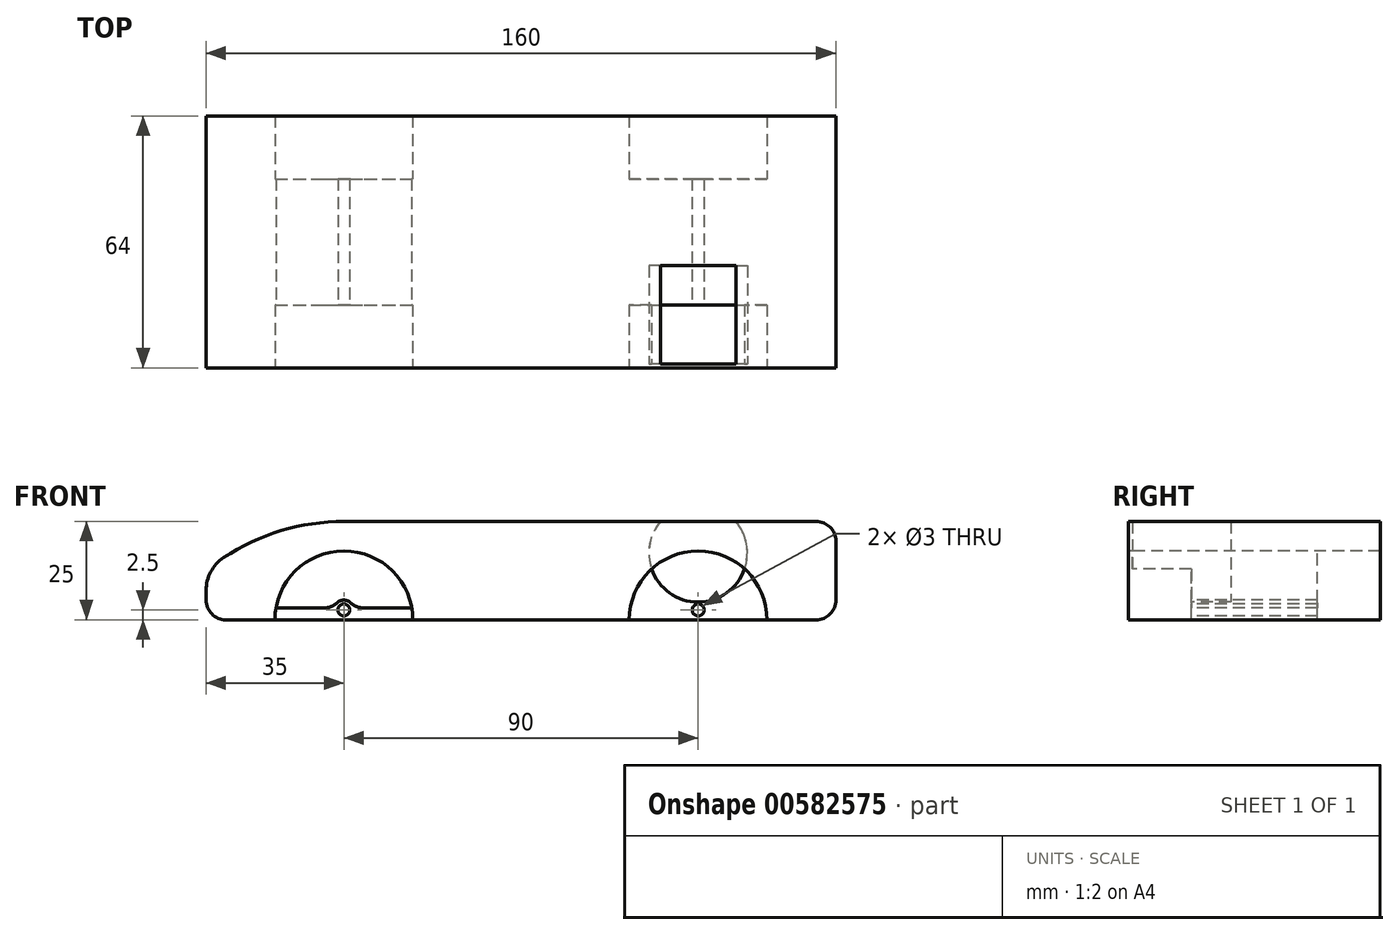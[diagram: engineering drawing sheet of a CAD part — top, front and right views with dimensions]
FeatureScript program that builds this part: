
annotation { "Feature Type Name" : "Feature", "Feature Type Description" : "" }
export const myFeature = defineFeature(function(context is Context, id is Id, definition is map)
    precondition{}
    {
        {
            var Q0;
            Q0=qCreatedBy(makeId("Front.planeOp"),FACE);
            var sketch = newSketch(context, id + "F0", { "sketchPlane" : qUnion([Q0])});
            skLineSegment(sketch, "E0.bottom", {"start": v(0, 0) * mm, "end": v(17.5, 0) * mm});
            skLineSegment(sketch, "E0.top", {"start": v(35, 25) * mm, "end": v(160, 25) * mm});
            skLineSegment(sketch, "E0.left", {"start": v(0, 0) * mm, "end": v(0, 12.5) * mm});
            skLineSegment(sketch, "E0.right", {"start": v(160, 0) * mm, "end": v(160, 25) * mm});
            skArc(sketch, "E1", {"start": v(52.5, 0) * mm, "mid": v(35, 17.5) * mm, "end": v(17.5, 0) * mm});
            skArc(sketch, "E2", {"start": v(142.5, 0) * mm, "mid": v(125, 17.5) * mm, "end": v(107.5, 0) * mm});
            skPoint(sketch, "E3", {"position": v(35, 25) * mm});
            skArc(sketch, "E4", {"start": v(35, 25) * mm, "mid": v(16.42, 21.78) * mm, "end": v(0, 12.5) * mm});
            skPoint(sketch, "E5.orphan", {"position": v(0, 25) * mm});
            skLineSegment(sketch, "E6.trimOffspring", {"start": v(52.5, 0) * mm, "end": v(107.5, 0) * mm});
            skLineSegment(sketch, "E7.trimOffspring", {"start": v(142.5, 0) * mm, "end": v(160, 0) * mm});
            skSolve(sketch);
        }
        {
            var Q0;
            Q0=makeQuery(id+"F0.imprint","IMPRINT",FACE,{"disambiguationData":[TD([[makeQuery(id+"F0.imprint","IMPRINT",EDGE,{"derivedFrom":sQuery(id+"F0.wireOp",EDGE,"E0.bottom")}),1.0]])]});
            extrude(context, id + "F1", {"entities" : qUnion([Q0]), "oppositeDirection" : true, "depth" : 64 * mm, "offsetDistance" : 25 * mm});
        }
        {
            var Q0;
            Q0=makeQuery(id+"F1.opExtrude","SWEPT_EDGE",EDGE,{"disambiguationData":[OSD([sQuery(id+"F0.wireOp",EDGE,"E0.top"),sQuery(id+"F0.wireOp",EDGE,"E0.right")])]});
            var Q1;
            Q1=makeQuery(id+"F1.opExtrude","SWEPT_EDGE",EDGE,{"disambiguationData":[OSD([sQuery(id+"F0.wireOp",EDGE,"E0.bottom"),sQuery(id+"F0.wireOp",EDGE,"E0.left")])]});
            var Q2;
            Q2=makeQuery(id+"F1.opExtrude","SWEPT_EDGE",EDGE,{"disambiguationData":[OSD([sQuery(id+"F0.wireOp",EDGE,"E0.right"),sQuery(id+"F0.wireOp",EDGE,"E7.trimOffspring")])]});
            fillet(context, id + "F2", {"entities" : qUnion([Q0, Q1, Q2]), "radius" : 5 * mm, "tangentPropagation" : true, "allowEdgeOverflow" : false});
        }
        {
            var Q0;
            Q0=makeQuery(id+"F1.opExtrude","SWEPT_EDGE",EDGE,{"disambiguationData":[OSD([sQuery(id+"F0.wireOp",EDGE,"E0.left"),sQuery(id+"F0.wireOp",EDGE,"E4")])]});
            fillet(context, id + "F3", {"entities" : qUnion([Q0]), "radius" : 10 * mm, "tangentPropagation" : true, "allowEdgeOverflow" : false});
        }
        {
            var Q0;
            Q0=qCreatedBy(makeId("Front.planeOp"),FACE);
            cPlane(context, id + "F4", {"entities" : qUnion([Q0]), "cplaneType" : CPlaneType.OFFSET, "offset" : 16 * mm, "oppositeDirection" : true, "width" : 150 * mm, "height" : 150 * mm});
        }
        {
            var Q0;
            Q0=qCreatedBy(id+"F4.planeOp",FACE);
            var sketch = newSketch(context, id + "F5", { "sketchPlane" : qUnion([Q0])});
            skArc(sketch, "E8.0", {"start": v(52.5, 0) * mm, "mid": v(52.44, 1.5) * mm, "end": v(52.24, 3) * mm});
            skLineSegment(sketch, "E9", {"start": v(17.5, 0) * mm, "end": v(52.5, 0) * mm});
            skLineSegment(sketch, "E10", {"start": v(17.76, 3) * mm, "end": v(32.55, 3) * mm});
            skCircle(sketch, "E11", {"center": v(35, 2.5) * mm, "radius": 1.5 * mm});
            skPoint(sketch, "E11.centerSnap0", {"position": v(35, 3) * mm});
            skArc(sketch, "E12", {"start": v(37.45, 3) * mm, "mid": v(35, 5) * mm, "end": v(32.55, 3) * mm});
            skLineSegment(sketch, "E13.trimOffspring", {"start": v(37.45, 3) * mm, "end": v(52.24, 3) * mm});
            skArc(sketch, "E14.trimOffspring", {"start": v(17.76, 3) * mm, "mid": v(17.56, 1.5) * mm, "end": v(17.5, 0) * mm});
            skArc(sketch, "E15.0", {"start": v(142.5, 0) * mm, "mid": v(125, 17.5) * mm, "end": v(107.5, 0) * mm});
            skLineSegment(sketch, "E16", {"start": v(107.5, 0) * mm, "end": v(142.5, 0) * mm});
            skCircle(sketch, "E17", {"center": v(125, 2.5) * mm, "radius": 1.5 * mm});
            skSolve(sketch);
        }
        {
            var Q0;
            Q0=makeQuery(id+"F5.imprint","IMPRINT",FACE,{"disambiguationData":[TD([[makeQuery(id+"F5.imprint","IMPRINT",EDGE,{"derivedFrom":sQuery(id+"F5.wireOp",EDGE,"E8.0")}),1.0]])]});
            var Q1;
            Q1=makeQuery(id+"F5.imprint","IMPRINT",FACE,{"disambiguationData":[TD([[makeQuery(id+"F5.imprint","IMPRINT",EDGE,{"derivedFrom":sQuery(id+"F5.wireOp",EDGE,"E15.0")}),1.0]])]});
            extrude(context, id + "F6", {"entities" : qUnion([Q0, Q1]), "operationType" : NewBodyOperationType.ADD, "oppositeDirection" : true, "depth" : 32 * mm, "offsetDistance" : 25 * mm});
        }
        {
            var Q0;
            Q0=makeQuery(id+"F6.opExtrude","SWEPT_EDGE",EDGE,{"disambiguationData":[OSD([sQuery(id+"F5.wireOp",EDGE,"E12"),sQuery(id+"F5.wireOp",EDGE,"E13.trimOffspring")])]});
            var Q1;
            Q1=makeQuery(id+"F6.opExtrude","SWEPT_EDGE",EDGE,{"disambiguationData":[OSD([sQuery(id+"F5.wireOp",EDGE,"E10"),sQuery(id+"F5.wireOp",EDGE,"E12")])]});
            fillet(context, id + "F7", {"entities" : qUnion([Q0, Q1]), "radius" : 5 * mm, "tangentPropagation" : true, "allowEdgeOverflow" : false});
        }
        {
            var Q0;
            Q0=qCreatedBy(id+"F4.planeOp",FACE);
            var sketch = newSketch(context, id + "F8", { "sketchPlane" : qUnion([Q0])});
            skArc(sketch, "E18.0", {"start": v(142.5, 0) * mm, "mid": v(125, 17.5) * mm, "end": v(107.5, 0) * mm});
            skCircle(sketch, "E19", {"center": v(125, 17) * mm, "radius": 12.5 * mm});
            skPoint(sketch, "E20", {"position": v(125, 2.5) * mm});
            skSolve(sketch);
        }
        {
            var Q0;
            {var subQ0=sQuery(id+"F8.wireOp",EDGE,"E19");var subQ1=sQuery(id+"F8.wireOp",EDGE,"E18.0");var subQ2=makeQuery(id+"F8.imprint","INTERSECT",VERTEX,{"disambiguationData":[OD(0.0)],"derivedFrom":[subQ1,subQ0]});Q0=makeQuery(id+"F8.imprint","IMPRINT",FACE,{"disambiguationData":[TD([[makeQuery(id+"F8.imprint","IMPRINT",EDGE,{"disambiguationData":[TD([[subQ2,1.0]])],"derivedFrom":subQ1}),-1.0]])]});}
            var Q1;
            {var subQ0=sQuery(id+"F8.wireOp",EDGE,"E19");var subQ1=sQuery(id+"F8.wireOp",EDGE,"E18.0");var subQ2=makeQuery(id+"F8.imprint","INTERSECT",VERTEX,{"disambiguationData":[OD(0.0)],"derivedFrom":[subQ1,subQ0]});Q1=makeQuery(id+"F8.imprint","IMPRINT",FACE,{"disambiguationData":[TD([[makeQuery(id+"F8.imprint","IMPRINT",EDGE,{"disambiguationData":[TD([[subQ2,1.0]])],"derivedFrom":subQ1}),1.0]])]});}
            extrude(context, id + "F9", {"entities" : qUnion([Q0, Q1]), "operationType" : NewBodyOperationType.REMOVE, "oppositeDirection" : true, "depth" : 10 * mm, "offsetDistance" : 25 * mm, "hasSecondDirection" : true, "secondDirectionOppositeDirection" : false, "secondDirectionDepth" : 15 * mm});
        }
    });
